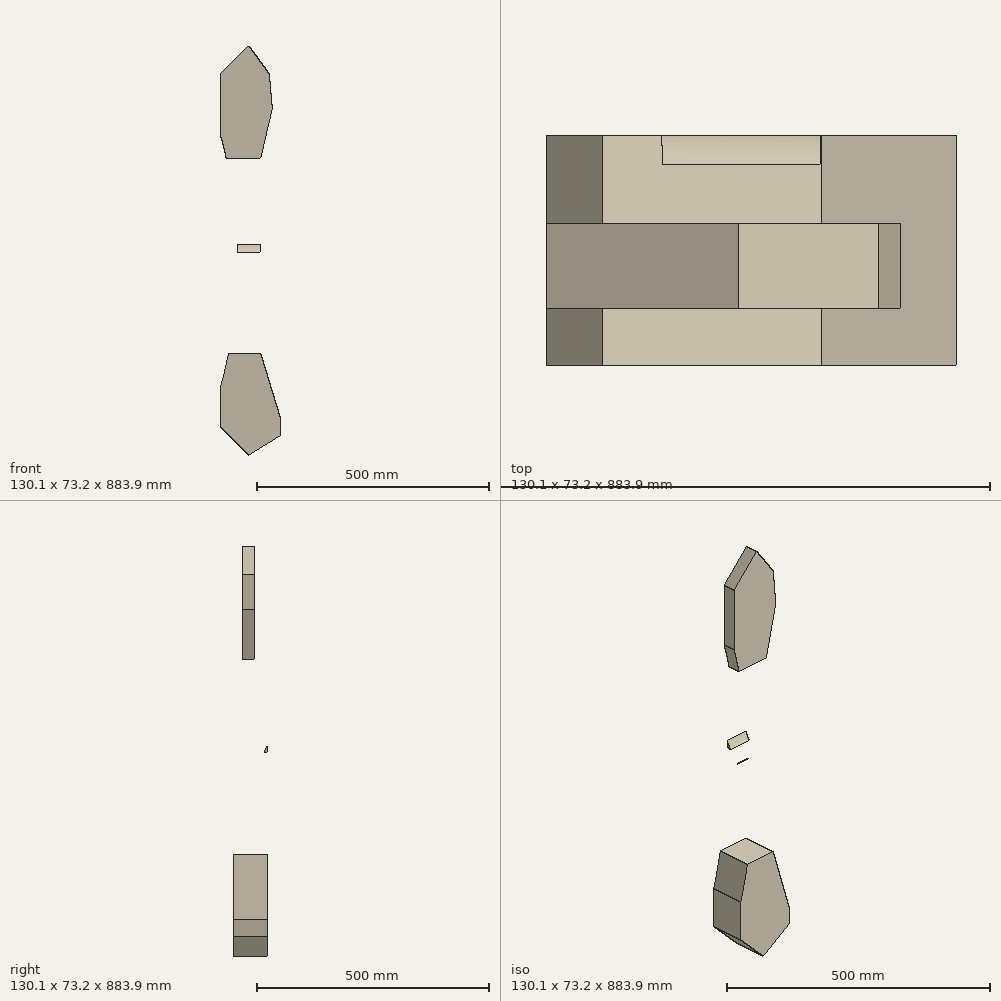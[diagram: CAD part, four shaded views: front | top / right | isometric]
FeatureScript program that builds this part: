
annotation { "Feature Type Name" : "Feature", "Feature Type Description" : "" }
export const myFeature = defineFeature(function(context is Context, id is Id, definition is map)
    precondition{}
    {
        {
            var Q0;
            Q0=qCreatedBy(makeId("Front.planeOp"),FACE);
            var sketch = newSketch(context, id + "F0", { "sketchPlane" : qUnion([Q0])});
            skLineSegment(sketch, "E0", {"start": v(-44.07, 96.96) * mm, "end": v(-44.07, -665.04) * mm});
            skLineSegment(sketch, "E1", {"start": v(-44.07, 96.96) * mm, "end": v(16.9, 96.96) * mm});
            skLineSegment(sketch, "E2", {"start": v(16.9, 96.96) * mm, "end": v(16.9, 157.92) * mm});
            skLineSegment(sketch, "E3", {"start": v(-44.07, -665.04) * mm, "end": v(16.9, -665.04) * mm});
            skLineSegment(sketch, "E4", {"start": v(16.9, -665.04) * mm, "end": v(16.9, -726) * mm});
            skLineSegment(sketch, "E5", {"start": v(16.9, -726) * mm, "end": v(-44.07, -665.04) * mm});
            skLineSegment(sketch, "E6", {"start": v(16.9, 157.92) * mm, "end": v(-44.07, 96.96) * mm});
            skLineSegment(sketch, "E7", {"start": v(16.9, 157.92) * mm, "end": v(61.4, 96.96) * mm});
            skLineSegment(sketch, "E8", {"start": v(61.4, 96.96) * mm, "end": v(68.19, 21.71) * mm});
            skLineSegment(sketch, "E9", {"start": v(68.19, 21.71) * mm, "end": v(43.02, -86.7) * mm});
            skLineSegment(sketch, "E10", {"start": v(43.02, -86.7) * mm, "end": v(43.02, -506.03) * mm});
            skLineSegment(sketch, "E11", {"start": v(43.02, -506.03) * mm, "end": v(86.01, -646.48) * mm});
            skLineSegment(sketch, "E12", {"start": v(86.01, -646.48) * mm, "end": v(86.01, -683.32) * mm});
            skLineSegment(sketch, "E13", {"start": v(86.01, -683.32) * mm, "end": v(16.9, -726) * mm});
            skSolve(sketch);
        }
        {
            var Q0;
            Q0=makeQuery(id+"F0.imprint","IMPRINT",FACE,{"disambiguationData":[TD([[makeQuery(id+"F0.imprint","IMPRINT",EDGE,{"derivedFrom":sQuery(id+"F0.wireOp",EDGE,"E1")}),1.0]])]});
            var Q1;
            Q1=makeQuery(id+"F0.imprint","IMPRINT",FACE,{"disambiguationData":[TD([[makeQuery(id+"F0.imprint","IMPRINT",EDGE,{"derivedFrom":sQuery(id+"F0.wireOp",EDGE,"E0")}),1.0]])]});
            var Q2;
            Q2=makeQuery(id+"F0.imprint","IMPRINT",FACE,{"disambiguationData":[TD([[makeQuery(id+"F0.imprint","IMPRINT",EDGE,{"derivedFrom":sQuery(id+"F0.wireOp",EDGE,"E3")}),-1.0]])]});
            extrude(context, id + "F1", {"entities" : qUnion([Q0, Q1, Q2]), "depth" : 30.48 * mm, "offsetDistance" : 30.48 * mm});
        }
        {
            var Q0;
            Q0=makeQuery(id+"F1.opExtrude","CAP_FACE",FACE,{"disambiguationData":[OSD([sQuery(id+"F0.wireOp",EDGE,"E0"),sQuery(id+"F0.wireOp",EDGE,"E5"),sQuery(id+"F0.wireOp",EDGE,"E6"),sQuery(id+"F0.wireOp",EDGE,"E7"),sQuery(id+"F0.wireOp",EDGE,"E8"),sQuery(id+"F0.wireOp",EDGE,"E9"),sQuery(id+"F0.wireOp",EDGE,"E10"),sQuery(id+"F0.wireOp",EDGE,"E11"),sQuery(id+"F0.wireOp",EDGE,"E12"),sQuery(id+"F0.wireOp",EDGE,"E13")])],"isStart":false});
            extrude(context, id + "F2", {"entities" : qUnion([Q0]), "operationType" : NewBodyOperationType.ADD, "depth" : 30.48 * mm, "offsetDistance" : 30.48 * mm});
        }
        {
            var Q0;
            Q0=makeQuery(id+"F2.opExtrude","CAP_FACE",FACE,{"disambiguationData":[OSD([sQuery(id+"F0.wireOp",EDGE,"E0"),sQuery(id+"F0.wireOp",EDGE,"E5"),sQuery(id+"F0.wireOp",EDGE,"E6"),sQuery(id+"F0.wireOp",EDGE,"E7"),sQuery(id+"F0.wireOp",EDGE,"E8"),sQuery(id+"F0.wireOp",EDGE,"E9"),sQuery(id+"F0.wireOp",EDGE,"E10"),sQuery(id+"F0.wireOp",EDGE,"E11"),sQuery(id+"F0.wireOp",EDGE,"E12"),sQuery(id+"F0.wireOp",EDGE,"E13")])],"isStart":false});
            extrude(context, id + "F3", {"entities" : qUnion([Q0]), "operationType" : NewBodyOperationType.ADD, "depth" : 30.48 * mm, "offsetDistance" : 30.48 * mm});
        }
        {
            var Q0;
            Q0=makeQuery(id+"F1.opExtrude","CAP_FACE",FACE,{"disambiguationData":[OSD([sQuery(id+"F0.wireOp",EDGE,"E0"),sQuery(id+"F0.wireOp",EDGE,"E5"),sQuery(id+"F0.wireOp",EDGE,"E6"),sQuery(id+"F0.wireOp",EDGE,"E7"),sQuery(id+"F0.wireOp",EDGE,"E8"),sQuery(id+"F0.wireOp",EDGE,"E9"),sQuery(id+"F0.wireOp",EDGE,"E10"),sQuery(id+"F0.wireOp",EDGE,"E11"),sQuery(id+"F0.wireOp",EDGE,"E12"),sQuery(id+"F0.wireOp",EDGE,"E13")])],"isStart":true});
            var sketch = newSketch(context, id + "F4", { "sketchPlane" : qUnion([Q0])});
            skArc(sketch, "E14", {"start": v(44.07, -34.15) * mm, "mid": v(7, -307.7) * mm, "end": v(44.07, -581.24) * mm});
            skPoint(sketch, "E14.startSnap0", {"position": v(14.37, -34.15) * mm});
            skSolve(sketch);
        }
        {
            var Q0;
            {var subQ0=sQuery(id+"F4.wireOp",EDGE,"E14");Q0=makeQuery(id+"F4.imprint","IMPRINT",FACE,{"disambiguationData":[TD([[makeQuery(id+"F4.imprint","IMPRINT",EDGE,{"derivedFrom":subQ0}),1.0]])]});}
            extrude(context, id + "F5", {"entities" : qUnion([Q0]), "operationType" : NewBodyOperationType.REMOVE, "oppositeDirection" : true, "depth" : 661.42 * mm, "offsetDistance" : 30.48 * mm});
        }
        {
            var Q0;
            {var subQ0=sQuery(id+"F0.wireOp",EDGE,"E10");Q0=makeQuery(id+"F3.boolean.opBoolean","MERGE",FACE,{"derivedFrom":[makeQuery(id+"F2.boolean.opBoolean","MERGE",FACE,{"derivedFrom":[makeQuery(id+"F1.opExtrude","SWEPT_FACE",FACE,{"disambiguationData":[OSD([subQ0])]}),makeQuery(id+"F2.opExtrude","SWEPT_FACE",FACE,{"disambiguationData":[OSD([subQ0])]})]}),makeQuery(id+"F3.opExtrude","SWEPT_FACE",FACE,{"disambiguationData":[OSD([subQ0])]})]});}
            var sketch = newSketch(context, id + "F6", { "sketchPlane" : qUnion([Q0])});
            skLineSegment(sketch, "E15", {"start": v(-91.44, -122.49) * mm, "end": v(-45.72, -122.49) * mm});
            skPoint(sketch, "E15.endSnap0", {"position": v(-45.72, -86.7) * mm});
            skLineSegment(sketch, "E16", {"start": v(-45.72, -122.49) * mm, "end": v(-45.72, -274.87) * mm});
            skLineSegment(sketch, "E17", {"start": v(-45.72, -274.87) * mm, "end": v(-91.44, -274.87) * mm});
            skSolve(sketch);
        }
        {
            var Q0;
            {var subQ0=sQuery(id+"F6.wireOp",EDGE,"E15");Q0=makeQuery(id+"F6.imprint","IMPRINT",FACE,{"disambiguationData":[TD([[makeQuery(id+"F6.imprint","IMPRINT",EDGE,{"derivedFrom":subQ0}),-1.0]])]});}
            extrude(context, id + "F7", {"entities" : qUnion([Q0]), "operationType" : NewBodyOperationType.REMOVE, "oppositeDirection" : true, "depth" : 222.5 * mm, "offsetDistance" : 30.48 * mm});
        }
        {
            var Q0;
            Q0=makeQuery(id+"F1.opExtrude","CAP_FACE",FACE,{"disambiguationData":[OSD([sQuery(id+"F0.wireOp",EDGE,"E0"),sQuery(id+"F0.wireOp",EDGE,"E5"),sQuery(id+"F0.wireOp",EDGE,"E6"),sQuery(id+"F0.wireOp",EDGE,"E7"),sQuery(id+"F0.wireOp",EDGE,"E8"),sQuery(id+"F0.wireOp",EDGE,"E9"),sQuery(id+"F0.wireOp",EDGE,"E10"),sQuery(id+"F0.wireOp",EDGE,"E11"),sQuery(id+"F0.wireOp",EDGE,"E12"),sQuery(id+"F0.wireOp",EDGE,"E13")])],"isStart":true});
            var sketch = newSketch(context, id + "F8", { "sketchPlane" : qUnion([Q0])});
            skLineSegment(sketch, "E18", {"start": v(-43.02, -86.7) * mm, "end": v(31.04, -86.7) * mm});
            skSolve(sketch);
        }
        {
            var Q0;
            {var subQ28=sQuery(id+"F8.wireOp",EDGE,"E18");Q0=makeQuery(id+"F8.imprint","IMPRINT",FACE,{"disambiguationData":[TD([[makeQuery(id+"F8.imprint","IMPRINT",EDGE,{"derivedFrom":subQ28}),1.0]])]});}
            extrude(context, id + "F9", {"entities" : qUnion([Q0]), "operationType" : NewBodyOperationType.REMOVE, "oppositeDirection" : true, "depth" : 46.33 * mm, "offsetDistance" : 30.48 * mm});
        }
        {
            var Q0;
            Q0=makeQuery(id+"F1.opExtrude","CAP_FACE",FACE,{"disambiguationData":[OSD([sQuery(id+"F0.wireOp",EDGE,"E0"),sQuery(id+"F0.wireOp",EDGE,"E5"),sQuery(id+"F0.wireOp",EDGE,"E6"),sQuery(id+"F0.wireOp",EDGE,"E7"),sQuery(id+"F0.wireOp",EDGE,"E8"),sQuery(id+"F0.wireOp",EDGE,"E9"),sQuery(id+"F0.wireOp",EDGE,"E10"),sQuery(id+"F0.wireOp",EDGE,"E11"),sQuery(id+"F0.wireOp",EDGE,"E12"),sQuery(id+"F0.wireOp",EDGE,"E13")])],"isStart":true});
            extrude(context, id + "F10", {"entities" : qUnion([Q0]), "operationType" : NewBodyOperationType.REMOVE, "oppositeDirection" : true, "depth" : 18.29 * mm, "offsetDistance" : 30.48 * mm});
        }
        {
            var Q0;
            {var subQ0=sQuery(id+"F0.wireOp",EDGE,"E10");Q0=makeQuery(id+"F3.boolean.opBoolean","MERGE",FACE,{"derivedFrom":[makeQuery(id+"F2.boolean.opBoolean","MERGE",FACE,{"derivedFrom":[makeQuery(id+"F1.opExtrude","SWEPT_FACE",FACE,{"disambiguationData":[OSD([subQ0])]}),makeQuery(id+"F2.opExtrude","SWEPT_FACE",FACE,{"disambiguationData":[OSD([subQ0])]})]}),makeQuery(id+"F3.opExtrude","SWEPT_FACE",FACE,{"disambiguationData":[OSD([subQ0])]})]});}
            var sketch = newSketch(context, id + "F11", { "sketchPlane" : qUnion([Q0])});
            skArc(sketch, "E19", {"start": v(-71.49, -306.98) * mm, "mid": v(-76.81, -292.48) * mm, "end": v(-91.44, -287.52) * mm});
            skLineSegment(sketch, "E20", {"start": v(-71.49, -306.98) * mm, "end": v(-71.49, -398.37) * mm});
            skPoint(sketch, "E21.endSnap0", {"position": v(-18.29, -296.37) * mm});
            skLineSegment(sketch, "E22", {"start": v(-44.45, -296.37) * mm, "end": v(-44.45, -398.37) * mm});
            skArc(sketch, "E23", {"start": v(-18.29, -285.65) * mm, "mid": v(-37.11, -293.8) * mm, "end": v(-44.45, -312.96) * mm});
            skArc(sketch, "E24", {"start": v(-39.28, -296.37) * mm, "mid": v(-20.1, -275.76) * mm, "end": v(-18.29, -247.66) * mm});
            skLineSegment(sketch, "E25", {"start": v(-44.45, -398.37) * mm, "end": v(-44.45, -506.03) * mm});
            skLineSegment(sketch, "E26", {"start": v(-44.45, -506.03) * mm, "end": v(-71.49, -506.03) * mm});
            skLineSegment(sketch, "E27", {"start": v(-71.49, -506.03) * mm, "end": v(-71.49, -398.37) * mm});
            skSolve(sketch);
        }
        {
            var Q0;
            {var subQ0=sQuery(id+"F0.wireOp",EDGE,"E11");var subQ1=sQuery(id+"F0.wireOp",EDGE,"E10");var subQ2=sQuery(id+"F0.wireOp",EDGE,"E5");var subQ3=sQuery(id+"F0.wireOp",EDGE,"E0");var subQ4=sQuery(id+"F0.wireOp",EDGE,"E12");var subQ5=sQuery(id+"F0.wireOp",EDGE,"E13");Q0=makeQuery(id+"F7.boolean.opBoolean","SPLIT",FACE,{"disambiguationData":[TD([makeQuery(id+"F1.opExtrude","SWEPT_FACE",FACE,{"disambiguationData":[OSD([subQ2])]})])],"derivedFrom":makeQuery(id+"F3.opExtrude","CAP_FACE",FACE,{"disambiguationData":[OSD([subQ3,subQ2,sQuery(id+"F0.wireOp",EDGE,"E6"),sQuery(id+"F0.wireOp",EDGE,"E7"),sQuery(id+"F0.wireOp",EDGE,"E8"),sQuery(id+"F0.wireOp",EDGE,"E9"),subQ1,subQ0,subQ4,subQ5])],"isStart":false})});}
            var sketch = newSketch(context, id + "F12", { "sketchPlane" : qUnion([Q0])});
            skArc(sketch, "E28", {"start": v(43.02, -293.7) * mm, "mid": v(27.03, -299.68) * mm, "end": v(26.6, -316.75) * mm});
            skArc(sketch, "E29", {"start": v(43.02, -390.45) * mm, "mid": v(35.34, -353.48) * mm, "end": v(26.6, -316.75) * mm});
            skSolve(sketch);
        }
        {
            var Q0;
            {var subQ0=sQuery(id+"F12.wireOp",EDGE,"E28");Q0=makeQuery(id+"F12.imprint","IMPRINT",FACE,{"disambiguationData":[TD([[makeQuery(id+"F12.imprint","IMPRINT",EDGE,{"derivedFrom":subQ0}),1.0]])]});}
            extrude(context, id + "F13", {"entities" : qUnion([Q0]), "operationType" : NewBodyOperationType.REMOVE, "oppositeDirection" : true, "depth" : 296.27 * mm, "offsetDistance" : 30.48 * mm});
        }
        {
            var Q0;
            {var subQ6=sQuery(id+"F11.wireOp",EDGE,"E19");Q0=makeQuery(id+"F11.imprint","IMPRINT",FACE,{"disambiguationData":[TD([[makeQuery(id+"F11.imprint","IMPRINT",EDGE,{"derivedFrom":subQ6}),1.0]])]});}
            var Q1;
            {var subQ0=sQuery(id+"F11.wireOp",EDGE,"E23");var subQ1=makeQuery(id+"F10.boolean.opBoolean","COPY",EDGE,{"derivedFrom":makeQuery(id+"F10.opExtrude","CAP_EDGE",EDGE,{"disambiguationData":[OSD([sQuery(id+"F0.wireOp",EDGE,"E10")])],"isStart":false})});var subQ2=makeQuery(id+"F11.imprint","INTERSECT",VERTEX,{"derivedFrom":[subQ1,subQ0]});Q1=makeQuery(id+"F11.imprint","IMPRINT",FACE,{"disambiguationData":[TD([[makeQuery(id+"F11.imprint","IMPRINT",EDGE,{"disambiguationData":[TD([[subQ2,-1.0]])],"derivedFrom":subQ0}),-1.0]])]});}
            var Q2;
            {var subQ9=sQuery(id+"F11.wireOp",EDGE,"E25");Q2=makeQuery(id+"F11.imprint","IMPRINT",FACE,{"disambiguationData":[TD([[makeQuery(id+"F11.imprint","IMPRINT",EDGE,{"derivedFrom":subQ9}),1.0]])]});}
            var Q3;
            {var subQ0=sQuery(id+"F11.wireOp",EDGE,"E24");var subQ1=sQuery(id+"F11.wireOp",EDGE,"E23");var subQ2=makeQuery(id+"F11.imprint","INTERSECT",VERTEX,{"disambiguationData":[OD(0.0)],"derivedFrom":[subQ1,subQ0]});Q3=makeQuery(id+"F11.imprint","IMPRINT",FACE,{"disambiguationData":[TD([[makeQuery(id+"F11.imprint","IMPRINT",EDGE,{"disambiguationData":[TD([[subQ2,1.0]])],"derivedFrom":subQ1}),1.0]])]});}
            extrude(context, id + "F14", {"entities" : qUnion([Q0, Q1, Q2, Q3]), "operationType" : NewBodyOperationType.REMOVE, "oppositeDirection" : true, "depth" : 86.26 * mm, "offsetDistance" : 30.48 * mm});
        }
        {
            var Q0;
            {var subQ58=sQuery(id+"F0.wireOp",EDGE,"E10");var subQ59=sQuery(id+"F0.wireOp",EDGE,"E9");var subQ60=sQuery(id+"F0.wireOp",EDGE,"E8");var subQ61=sQuery(id+"F0.wireOp",EDGE,"E6");var subQ62=sQuery(id+"F0.wireOp",EDGE,"E7");var subQ63=sQuery(id+"F0.wireOp",EDGE,"E0");Q0=makeQuery(id+"F7.boolean.opBoolean","SPLIT",FACE,{"disambiguationData":[TD([makeQuery(id+"F1.opExtrude","SWEPT_FACE",FACE,{"disambiguationData":[OSD([subQ61])]})])],"derivedFrom":makeQuery(id+"F3.opExtrude","CAP_FACE",FACE,{"disambiguationData":[OSD([subQ63,sQuery(id+"F0.wireOp",EDGE,"E5"),subQ61,subQ62,subQ60,subQ59,subQ58,sQuery(id+"F0.wireOp",EDGE,"E11"),sQuery(id+"F0.wireOp",EDGE,"E12"),sQuery(id+"F0.wireOp",EDGE,"E13")])],"isStart":false})});}
            extrude(context, id + "F15", {"entities" : qUnion([Q0]), "operationType" : NewBodyOperationType.REMOVE, "oppositeDirection" : true, "depth" : 18.29 * mm, "offsetDistance" : 30.48 * mm});
        }
    });
